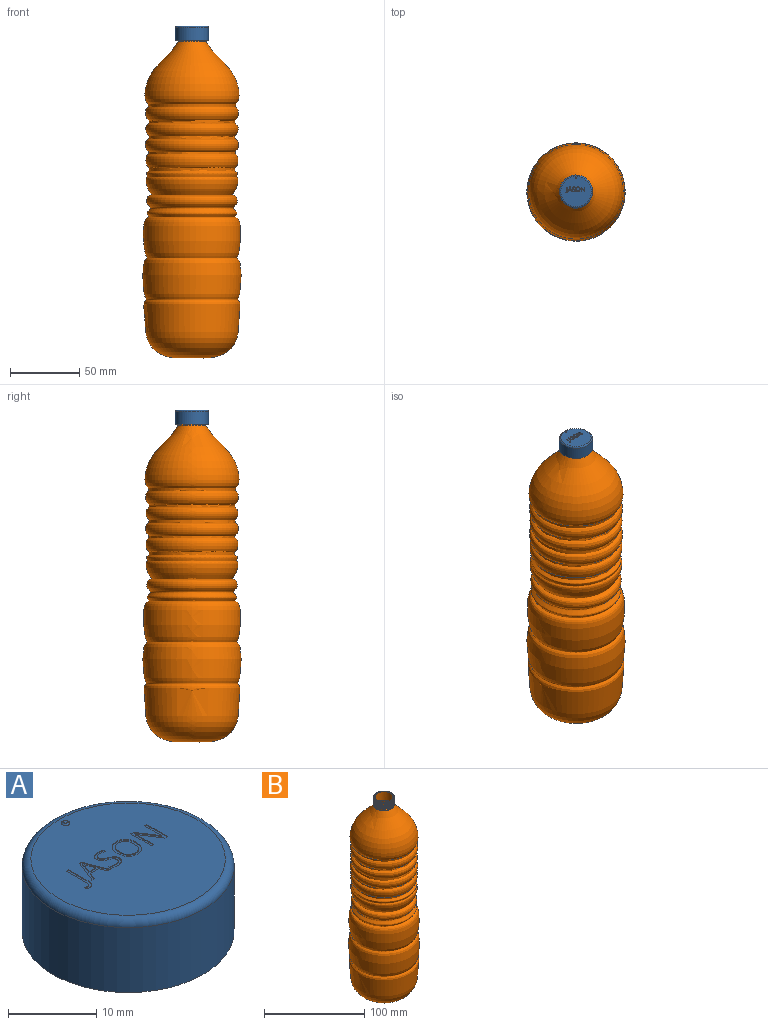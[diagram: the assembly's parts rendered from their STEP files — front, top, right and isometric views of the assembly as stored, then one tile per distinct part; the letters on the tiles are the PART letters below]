
ASSEMBLY  parts=2 mates=1
PART A: 99 faces, bbox 26.3x26.3x10.6 mm
  f0: plane 22x22mm, normal (0,0,1), area 359.5mm2, adj f5,f11,f12,f13,f14,f15,f16,f17
  f1: cylinder r=11mm len=22mm, axis (0,0,1), area 298.8mm2, adj f2,f4,f7,f8,f9,f10
  f2: plane 22.26x21.81mm, normal (0,0,-1), area 369.5mm2, adj f1,f8,f9,f10
  f3: cylinder r=12mm len=24mm, axis (0,0,1), area 678.6mm2, adj f4,f5
  f4: plane 24x24mm, normal (0,0,-1), area 72.2mm2, adj f1,f3,f6,f7,f9
  f5: torus R=11mm, axis (0,0,1), area 114.8mm2, adj f0,f3
  f6: cylinder r=11.01mm len=0.89mm, axis (0,0,1), area 0mm2, adj f4,f7,f9
  f7: plane 0.99x0.58mm, normal (0,-1,0), area 0.3mm2, adj f1,f4,f6,f9,f10
  f8: plane 0.02x0.01mm, normal (0,1,0), area 0mm2, adj f1,f2,f9
  f9: bspline ~25.43x22.02mm, area 248.4mm2, adj f1,f2,f4,f6,f7,f8,f10
  f10: bspline ~25.43x22.02mm, area 232.6mm2, adj f1,f2,f7,f9
  f11: extruded ~0.68x0.32mm, area 0.1mm2, adj f0,f12,f35,f36
  f12: extruded ~0.55x0.2mm, area 0.1mm2, adj f0,f11,f13,f36
  f13: extruded ~0.71x0.4mm, area 0.1mm2, adj f0,f12,f14,f36
  f14: extruded ~0.46x0.2mm, area 0.1mm2, adj f0,f13,f15,f36
  f15: extruded ~0.21x0.2mm, area 0mm2, adj f0,f14,f16,f36
  f16: extruded ~0.28x0.1mm, area 0mm2, adj f0,f15,f17,f36
  f17: extruded ~0.36x0.17mm, area 0mm2, adj f0,f16,f18,f36
  f18: extruded ~0.48x0.13mm, area 0.1mm2, adj f0,f17,f19,f36
  f19: extruded ~0.79x0.17mm, area 0.1mm2, adj f0,f18,f20,f36
  f20: plane 0.33x0.12mm, normal (-0.94,0.34,0), area 0mm2, adj f0,f19,f21,f36
  f21: extruded ~0.9x0.18mm, area 0.1mm2, adj f0,f20,f22,f36
  f22: extruded ~0.76x0.23mm, area 0.1mm2, adj f0,f21,f23,f36
  f23: extruded ~0.61x0.29mm, area 0.1mm2, adj f0,f22,f24,f36
  f24: extruded ~0.59x0.2mm, area 0.1mm2, adj f0,f23,f25,f36
  f25: extruded ~0.66x0.39mm, area 0.1mm2, adj f0,f24,f26,f36
  f26: extruded ~0.49x0.21mm, area 0.1mm2, adj f0,f25,f27,f36
  f27: extruded ~0.23x0.2mm, area 0mm2, adj f0,f26,f28,f36
  f28: extruded ~0.28x0.1mm, area 0mm2, adj f0,f27,f29,f36
  f29: extruded ~0.41x0.19mm, area 0mm2, adj f0,f28,f30,f36
  f30: extruded ~0.58x0.15mm, area 0.1mm2, adj f0,f29,f31,f36
  f31: extruded ~0.47x0.1mm, area 0mm2, adj f0,f30,f32,f36
  f32: extruded ~0.44x0.14mm, area 0mm2, adj f0,f31,f33,f36
  f33: plane 0.37x0.1mm, normal (1,0,0), area 0mm2, adj f0,f32,f34,f36
  f34: extruded ~0.9x0.15mm, area 0.1mm2, adj f0,f33,f35,f36
  f35: extruded ~0.86x0.24mm, area 0.1mm2, adj f0,f11,f34,f36
  f36: plane 3.39x2.08mm, normal (0,0,1), area 2.5mm2, adj f11,f12,f13,f14,f15,f16,f17,f18
  f37: plane 0.44x0.1mm, normal (0,1,0), area 0mm2, adj f0,f38,f51,f52
  f38: plane 3.3x0.1mm, normal (-1,0,0), area 0.3mm2, adj f0,f37,f39,f52
  f39: plane 0.36x0.1mm, normal (0,-1,0), area 0mm2, adj f0,f38,f40,f52
  f40: plane 1.89x0.1mm, normal (1,0,0), area 0.2mm2, adj f0,f39,f41,f52
  f41: extruded ~0.47x0.1mm, area 0mm2, adj f0,f40,f42,f52
  f42: extruded ~0.39x0.1mm, area 0mm2, adj f0,f41,f43,f52
  f43: plane 0.1x0.02mm, normal (0,-1,0), area 0mm2, adj f0,f42,f44,f52
  f44: plane 2.76x1.8mm, normal (-0.84,-0.55,0), area 0.3mm2, adj f0,f43,f45,f52
  f45: plane 0.43x0.1mm, normal (0,-1,0), area 0mm2, adj f0,f44,f46,f52
  f46: plane 3.3x0.1mm, normal (1,0,0), area 0.3mm2, adj f0,f45,f47,f52
  f47: plane 0.35x0.1mm, normal (0,1,0), area 0mm2, adj f0,f46,f48,f52
  f48: plane 1.87x0.1mm, normal (-1,0,0), area 0.2mm2, adj f0,f47,f49,f52
  f49: extruded ~0.89x0.1mm, area 0.1mm2, adj f0,f48,f50,f52
  f50: plane 0.1x0.02mm, normal (0,1,0), area 0mm2, adj f0,f49,f51,f52
  f51: plane 2.77x1.8mm, normal (0.84,0.55,0), area 0.3mm2, adj f0,f37,f50,f52
  f52: plane 3.3x2.58mm, normal (0,0,1), area 3.6mm2, adj f37,f38,f39,f40,f41,f42,f43,f44
  f53: plane 1.02x0.38mm, normal (0.94,0.35,0), area 0.1mm2, adj f54,f65,f66,f95
  f54: plane 1.07x0.1mm, normal (0,-1,0), area 0.1mm2, adj f53,f55,f66,f95
  f55: plane 1.02x0.39mm, normal (-0.94,0.35,0), area 0.1mm2, adj f54,f56,f66,f95
  f56: extruded ~0.48x0.14mm, area 0mm2, adj f55,f65,f66,f95
  f57: plane 1.05x0.41mm, normal (0.93,0.36,0), area 0.1mm2, adj f0,f58,f64,f66
  f58: plane 0.4x0.1mm, normal (0,1,0), area 0mm2, adj f0,f57,f59,f66
  f59: plane 3.31x1.3mm, normal (-0.93,-0.36,0), area 0.4mm2, adj f0,f58,f60,f66
  f60: plane 0.32x0.1mm, normal (0,-1,0), area 0mm2, adj f0,f59,f61,f66
  f61: plane 3.31x1.3mm, normal (0.93,-0.37,0), area 0.4mm2, adj f0,f60,f62,f66
  f62: plane 0.39x0.1mm, normal (0,1,0), area 0mm2, adj f0,f61,f63,f66
  f63: plane 1.05x0.41mm, normal (-0.93,0.36,0), area 0.1mm2, adj f0,f62,f64,f66
  f64: plane 1.32x0.1mm, normal (0,1,0), area 0.1mm2, adj f0,f57,f63,f66
  f65: extruded ~0.48x0.15mm, area 0mm2, adj f53,f56,f66,f95
  f66: plane 3.31x2.92mm, normal (0,0,1), area 2.8mm2, adj f53,f54,f55,f56,f57,f58,f59,f60
  f67: extruded ~1.02x0.29mm, area 0.1mm2, adj f68,f82,f83,f96
  f68: extruded ~1.01x0.29mm, area 0.1mm2, adj f67,f69,f83,f96
  f69: extruded ~0.83x0.35mm, area 0.1mm2, adj f68,f70,f83,f96
  f70: extruded ~0.82x0.34mm, area 0.1mm2, adj f69,f71,f83,f96
  f71: extruded ~1.01x0.28mm, area 0.1mm2, adj f70,f72,f83,f96
  f72: extruded ~1.02x0.28mm, area 0.1mm2, adj f71,f73,f83,f96
  f73: extruded ~0.83x0.35mm, area 0.1mm2, adj f72,f82,f83,f96
  f74: extruded ~1.25x0.4mm, area 0.1mm2, adj f0,f75,f81,f83
  f75: extruded ~1.25x0.4mm, area 0.1mm2, adj f0,f74,f76,f83
  f76: extruded ~1.11x0.45mm, area 0.1mm2, adj f0,f75,f77,f83
  f77: extruded ~1.13x0.44mm, area 0.1mm2, adj f0,f76,f78,f83
  f78: extruded ~1.25x0.4mm, area 0.1mm2, adj f0,f77,f79,f83
  f79: extruded ~1.26x0.4mm, area 0.1mm2, adj f0,f78,f80,f83
  f80: extruded ~1.12x0.45mm, area 0.1mm2, adj f0,f79,f81,f83
  f81: extruded ~1.11x0.45mm, area 0.1mm2, adj f0,f74,f80,f83
  f82: extruded ~0.83x0.35mm, area 0.1mm2, adj f67,f73,f83,f96
  f83: plane 3.4x3.03mm, normal (0,0,1), area 3.4mm2, adj f67,f68,f69,f70,f71,f72,f73,f74
  f84: extruded ~0.33x0.1mm, area 0mm2, adj f0,f85,f93,f94
  f85: extruded ~0.62x0.24mm, area 0.1mm2, adj f0,f84,f86,f94
  f86: extruded ~0.66x0.22mm, area 0.1mm2, adj f0,f85,f87,f94
  f87: plane 3.27x0.1mm, normal (-1,0,0), area 0.3mm2, adj f0,f86,f88,f94
  f88: plane 0.38x0.1mm, normal (0,-1,0), area 0mm2, adj f0,f87,f89,f94
  f89: plane 3.3x0.1mm, normal (1,0,0), area 0.3mm2, adj f0,f88,f90,f94
  f90: extruded ~0.39x0.12mm, area 0mm2, adj f0,f89,f91,f94
  f91: extruded ~0.34x0.14mm, area 0mm2, adj f0,f90,f92,f94
  f92: extruded ~0.33x0.1mm, area 0mm2, adj f0,f91,f93,f94
  f93: plane 0.33x0.1mm, normal (1,0,0), area 0mm2, adj f0,f84,f92,f94
  f94: plane 4.17x1.17mm, normal (0,0,1), area 1.8mm2, adj f84,f85,f86,f87,f88,f89,f90,f91
  f95: plane 1.5x1.07mm, normal (0,0,1), area 0.8mm2, adj f53,f54,f55,f56,f65
  f96: plane 2.72x2.22mm, normal (0,0,1), area 5mm2, adj f67,f68,f69,f70,f71,f72,f73,f82
  f97: plane 0.6x0.6mm, normal (0,0,1), area 0.3mm2, adj f98
  f98: cone r=0.3mm half-angle=45deg, axis (0,0,-1), area 0.7mm2, adj f0,f97
PART B: 11 faces, bbox 109x109x277.7 mm
  f0: cylinder r=9.99mm len=19.98mm, axis (0,0,-1), area 314.5mm2, adj f1,f2,f6,f7,f9,f10
  f1: revolved ~20.72x10.36mm, area 1.5mm2, adj f0,f5,f6
  f2: plane 20.01x20mm, normal (0,0,1), area 59.7mm2, adj f0,f4,f7,f8
  f3: revolved ~227.46x69.04mm, area 43530.6mm2, adj f4
  f4: cylinder r=8.99mm len=17.98mm, axis (0,0,-1), area 581.6mm2, adj f2,f3
  f5: plane 40.57x40.54mm, normal (0,-1,0), area 0.1mm2, adj f1,f6,f7
  f6: bspline ~21.18x21.18mm, area 244.3mm2, adj f0,f1,f5,f7,f9
  f7: bspline ~24.47x21.2mm, area 234.9mm2, adj f0,f2,f5,f6,f8
  f8: cone r=9.99mm half-angle=57deg, axis (0,0,-1), area 15.6mm2, adj f2,f7,f9,f10
  f9: cone r=10.6mm half-angle=51.9deg, axis (0,0,1), area 16.7mm2, adj f0,f6,f8,f10
  f10: plane 0.87x0.53mm, normal (-0.87,-0.5,0), area 0.3mm2, adj f0,f8,f9
PLACE A t=(126.32,51.65,-26.4)mm
PLACE B t=(43.79,51.65,-103.94)mm
MATE fastened A.f1 <-> B.f0  axis (0,0,1) through (126.32,51.65,-27.4)mm
